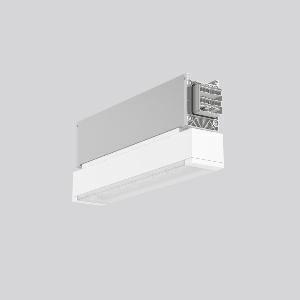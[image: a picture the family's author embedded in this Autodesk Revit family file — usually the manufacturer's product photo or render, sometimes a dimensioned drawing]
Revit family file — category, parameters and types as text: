
# Revit family: linedo_module_rf_9503rf_760_409_00c_ee49
name_source: partatom
category: Lighting Fixtures
units: mm (PartAtom-declared; Revit-internal decimal feet)

## family parameters
Cut with Voids When Loaded = No
Host = Face
Light Source = No
Part Type = Normal
Room Calculation Point = No
Round Connector Dimension = Use Diameter
Shared = No

## types (1)
- LINEDO Module RF (1 x LED Modul 763, 460 lm, 6300)
    Apparent Load = 7 VA
    CIE Flux Codes = 48 82 98 99 100
    Color Rendering = 70
    Color Temperature = 6300
    Default Elevation = 1800 mm
    Description = LINEDO, 6,5 W, 460 lm, 763, aluminium, on/off
Continuous line luminaire, L 342 B 58 H 131, CBS, emergency-460 lm, AC-Control
    Height = 131 mm
    Lamp = 1 x LED Modul 763
    Lamp Light Flux = 460 lm
    Lamp count = 1
    Length = 342 mm
    Lifetime = 50000 h
    Luminous efficacy = 71 lm/W
    Manufacturer = RZB
    ModVariant = No
    Model = 9503RF.760.409.00C
    Mounting Place = Ceiling
    Mounting Type = Surface mounted
    Number of Poles = 1
    OnlyDefault = Yes
    Power Factor = 1
    Product Name = LINEDO Module RF
    Product group = Surface mounted continuous line luminaire system
    ProductGroupID = 310
    Protection Class = Protection class I
    Protection Degree = IP 54
    RLX_Detail_Level = 1
    RLX_Emergency_Light_Flux = 460 lm
    RLX_Emergency_Type = 3
    RLX_Emergency_Type_DB = Yes
    RlxData = <blob elided: 32497 chars, md5=5cf27766>
    Socket = socket
    Standby Power = 0 W
    System Light Flux = 460 lm
    System Power = 7 W
    Type Comments = Product without accessories
    Type Image = 9503rf.760.430.00c.jpg
    URL = http://relux.com
    VarID = ---
    Voltage = 230 V
    Voltage Range = 220-240 V
    Weight = 0.00 kg
    Width = 58 mm

## geometry (parser evidence)
native form markers: Blend x4, Sweep x11
no freeform markers — native parametric forms only
